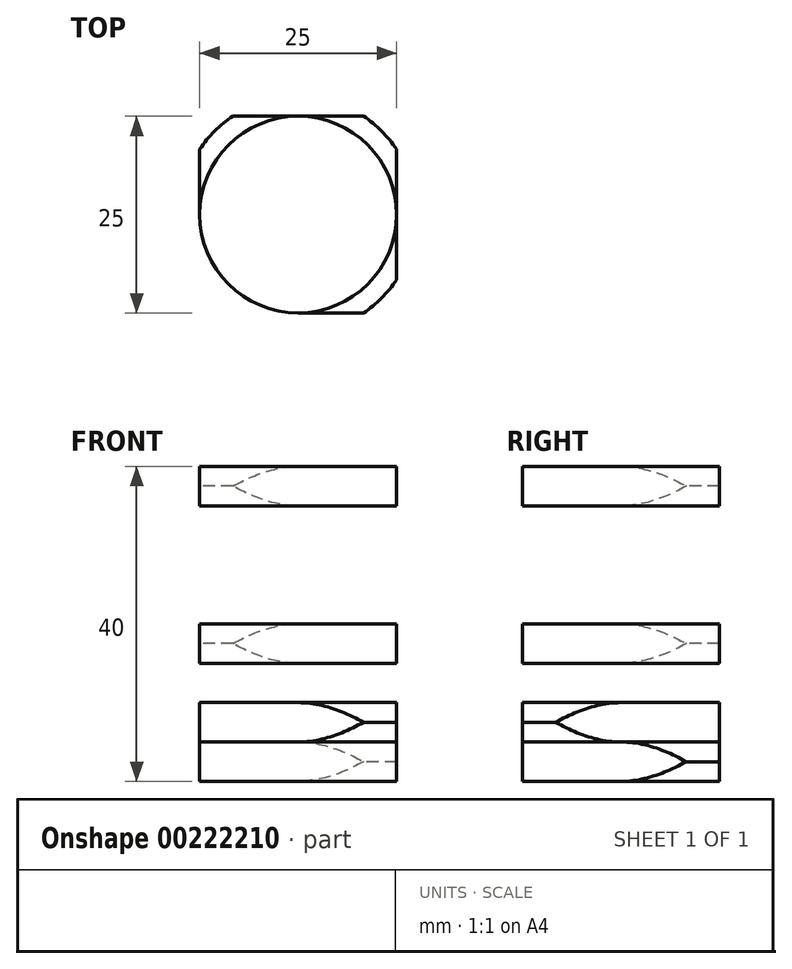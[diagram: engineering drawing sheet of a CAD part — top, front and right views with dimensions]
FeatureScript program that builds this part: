
annotation { "Feature Type Name" : "Feature", "Feature Type Description" : "" }
export const myFeature = defineFeature(function(context is Context, id is Id, definition is map)
    precondition{}
    {
        {
            var Q0;
            Q0=qCreatedBy(makeId("Top.planeOp"),FACE);
            var sketch = newSketch(context, id + "F0", { "sketchPlane" : qUnion([Q0])});
            skCircle(sketch, "E0", {"center": v(0, 0) * mm, "radius": 12.5 * mm});
            skLineSegment(sketch, "E1.bottom", {"start": v(12.5, 12.5) * mm, "end": v(-12.5, 12.5) * mm});
            skLineSegment(sketch, "E1.top", {"start": v(12.5, -12.5) * mm, "end": v(-12.5, -12.5) * mm});
            skLineSegment(sketch, "E1.left", {"start": v(12.5, 12.5) * mm, "end": v(12.5, -12.5) * mm});
            skLineSegment(sketch, "E1.right", {"start": v(-12.5, 12.5) * mm, "end": v(-12.5, -12.5) * mm});
            skArc(sketch, "E2", {"start": v(12.5, 8.3) * mm, "mid": v(10.6, 10.6) * mm, "end": v(8.3, 12.5) * mm});
            skSolve(sketch);
        }
        {
            var Q0;
            {var subQ0=sQuery(id+"F0.wireOp",EDGE,"E0");var subQ1=makeQuery(id+"F0.imprint","INTERSECT",VERTEX,{"derivedFrom":[subQ0,sQuery(id+"F0.wireOp",EDGE,"E1.bottom")]});Q0=makeQuery(id+"F0.imprint","IMPRINT",FACE,{"disambiguationData":[TD([[makeQuery(id+"F0.imprint","IMPRINT",EDGE,{"disambiguationData":[TD([[subQ1,1.0]])],"derivedFrom":subQ0}),1.0]])]});}
            var Q1;
            {var subQ5=sQuery(id+"F0.wireOp",EDGE,"E2");Q1=makeQuery(id+"F0.imprint","IMPRINT",FACE,{"disambiguationData":[TD([[makeQuery(id+"F0.imprint","IMPRINT",EDGE,{"derivedFrom":subQ5}),1.0]])]});}
            extrude(context, id + "F1", {"entities" : qUnion([Q0, Q1]), "endBound" : BoundingType.SYMMETRIC, "depth" : 5 * mm});
        }
        {
            var Q0;
            Q0=makeQuery(id+"F1.opExtrude","CAP_FACE",FACE,{"disambiguationData":[OSD([sQuery(id+"F0.wireOp",EDGE,"E0"),sQuery(id+"F0.wireOp",EDGE,"E1.bottom"),sQuery(id+"F0.wireOp",EDGE,"E1.left"),sQuery(id+"F0.wireOp",EDGE,"E2")])],"isStart":false});
            var sketch = newSketch(context, id + "F2", { "sketchPlane" : qUnion([Q0])});
            skCircle(sketch, "E3.0", {"center": v(0, 0) * mm, "radius": 12.5 * mm});
            skLineSegment(sketch, "E4", {"start": v(0, 12.5) * mm, "end": v(12.5, 0) * mm});
            skSolve(sketch);
        }
        {
            var Q0;
            Q0=makeQuery(id+"F1.opExtrude","CAP_FACE",FACE,{"disambiguationData":[OSD([sQuery(id+"F0.wireOp",EDGE,"E0"),sQuery(id+"F0.wireOp",EDGE,"E1.bottom"),sQuery(id+"F0.wireOp",EDGE,"E1.left"),sQuery(id+"F0.wireOp",EDGE,"E2")])],"isStart":true});
            var sketch = newSketch(context, id + "F3", { "sketchPlane" : qUnion([Q0])});
            skCircle(sketch, "E5.0", {"center": v(0, 0) * mm, "radius": 12.5 * mm});
            skLineSegment(sketch, "E6", {"start": v(12.5, 0) * mm, "end": v(0, -12.5) * mm});
            skSolve(sketch);
        }
        {
            var Q0;
            Q0=makeQuery(id+"F1.opExtrude","CAP_EDGE",EDGE,{"disambiguationData":[OSD([sQuery(id+"F0.wireOp",EDGE,"E2")])],"isStart":false});
            var Q1;
            Q1=makeQuery(id+"F1.opExtrude","CAP_EDGE",EDGE,{"disambiguationData":[OSD([sQuery(id+"F0.wireOp",EDGE,"E2")])],"isStart":true});
            chamfer(context, id + "F4", {"entities" : qUnion([Q0, Q1]), "width" : 2.5 * mm});
        }
        {
            var Q0;
            Q0=makeQuery(id+"F1.opExtrude","SWEPT_BODY",BODY,{"disambiguationData":[OSD([sQuery(id+"F0.wireOp",EDGE,"E0"),sQuery(id+"F0.wireOp",EDGE,"E1.bottom"),sQuery(id+"F0.wireOp",EDGE,"E1.left"),sQuery(id+"F0.wireOp",EDGE,"E2")])]});
            transform(context, id + "F5", {"entities" : qUnion([Q0]), "transformType" : TransformType.TRANSLATION_3D, "dx" : 0 * mm, "dy" : 0 * mm, "dz" : 5 * mm, "makeCopy" : true});
        }
        {
            var Q0;
            Q0=makeQuery(id+"F5.opPattern","COPY",BODY,{"derivedFrom":makeQuery(id+"F1.opExtrude","SWEPT_BODY",BODY,{"disambiguationData":[OSD([sQuery(id+"F0.wireOp",EDGE,"E0"),sQuery(id+"F0.wireOp",EDGE,"E1.bottom"),sQuery(id+"F0.wireOp",EDGE,"E1.left"),sQuery(id+"F0.wireOp",EDGE,"E2")])]}),"instanceName":"1"});
            var Q1;
            Q1=sQuery(id+"F2.wireOp",EDGE,"E3.0");
            transform(context, id + "F6", {"entities" : qUnion([Q0]), "transformType" : TransformType.ROTATION, "transformAxis" : qUnion([Q1]), "angle" : 90 * degree, "oppositeDirection" : true, "makeCopy" : false});
        }
        {
            var Q0;
            Q0=makeQuery(id+"F5.opPattern","COPY",BODY,{"derivedFrom":makeQuery(id+"F1.opExtrude","SWEPT_BODY",BODY,{"disambiguationData":[OSD([sQuery(id+"F0.wireOp",EDGE,"E0"),sQuery(id+"F0.wireOp",EDGE,"E1.bottom"),sQuery(id+"F0.wireOp",EDGE,"E1.left"),sQuery(id+"F0.wireOp",EDGE,"E2")])]}),"instanceName":"1"});
            transform(context, id + "F7", {"entities" : qUnion([Q0]), "transformType" : TransformType.TRANSLATION_3D, "dx" : 0 * mm, "dy" : 0 * mm, "dz" : 10 * mm, "makeCopy" : true});
        }
        {
            var Q0;
            Q0=makeQuery(id+"F7.opPattern","COPY",BODY,{"derivedFrom":makeQuery(id+"F5.opPattern","COPY",BODY,{"derivedFrom":makeQuery(id+"F1.opExtrude","SWEPT_BODY",BODY,{"disambiguationData":[OSD([sQuery(id+"F0.wireOp",EDGE,"E0"),sQuery(id+"F0.wireOp",EDGE,"E1.bottom"),sQuery(id+"F0.wireOp",EDGE,"E1.left"),sQuery(id+"F0.wireOp",EDGE,"E2")])]}),"instanceName":"1"}),"instanceName":"1"});
            var Q1;
            Q1=sQuery(id+"F3.wireOp",EDGE,"E5.0");
            transform(context, id + "F8", {"entities" : qUnion([Q0]), "transformType" : TransformType.ROTATION, "transformAxis" : qUnion([Q1]), "angle" : 180 * degree, "makeCopy" : false});
        }
        {
            var Q0;
            Q0=makeQuery(id+"F7.opPattern","COPY",BODY,{"derivedFrom":makeQuery(id+"F5.opPattern","COPY",BODY,{"derivedFrom":makeQuery(id+"F1.opExtrude","SWEPT_BODY",BODY,{"disambiguationData":[OSD([sQuery(id+"F0.wireOp",EDGE,"E0"),sQuery(id+"F0.wireOp",EDGE,"E1.bottom"),sQuery(id+"F0.wireOp",EDGE,"E1.left"),sQuery(id+"F0.wireOp",EDGE,"E2")])]}),"instanceName":"1"}),"instanceName":"1"});
            transform(context, id + "F9", {"entities" : qUnion([Q0]), "transformType" : TransformType.TRANSLATION_3D, "dx" : 0 * mm, "dy" : 0 * mm, "dz" : 20 * mm, "makeCopy" : true});
        }
    });
